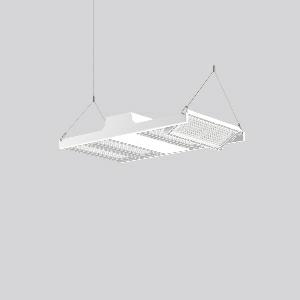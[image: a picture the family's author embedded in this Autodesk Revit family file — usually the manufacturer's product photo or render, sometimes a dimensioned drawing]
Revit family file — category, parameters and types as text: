
# Revit family: light_case_921688_002_76_3383
name_source: partatom
category: Lighting Fixtures
units: mm (PartAtom-declared; Revit-internal decimal feet)

## family parameters
Cut with Voids When Loaded = No
Host = Face
Light Source = No
Part Type = Normal
Room Calculation Point = No
Round Connector Dimension = Use Diameter
Shared = No

## types (1)
- LIGHT CASE (1 x LED Modul 840, 8900 lm, 4000)
    Apparent Load = 225 VA
    CIE Flux Codes = 81 98 100 100 100
    Color Rendering = 80
    Color Temperature = 4000
    Default Elevation = 1800 mm
    Description = Series: LIGHT CASE
Flat highbay luminaire for chain or cable suspension with 4 LED modules that can be swivelled. Housing: die cast aluminium and sheet steel, powder-coated. Optimised thermal management thanks to special luminaire design. Self-cleaning heat sink for constant heat dissipation. Cover: plastic (polycarbonate, shockproof), with integrated four-row lens system. LED modules can be swivelled ± 30° for optimum illumination. Suitable for chain or steel cable suspension (to be provided on site). With 5-pin connection terminal (1.5 m). With integrated movement sensor and light sensor for daylight detection on request. Ball impact proof in accordance with DIN 18032-03 (except steel cable suspension). Luminaire with limited surface temperature in accordance with EN 60598-2-24 for use in environments in which a deposit of conductive dust on the luminaire can be expected. 
Colour: white
Length: 680 mm
Width: 397 mm
Height: 110 mm
Lamp: LED
Socket: without socket
Colour temperature: 4000K
Colour rendering index (CRI): 80
System power: 225 W
Rated luminous flux: 35600 lm
Luminous efficiency: 158 lm/W
Control gear: Converter, dimmable, DALI
Protection class: I
Type of protection: IP 65
    Height = 110 mm
    Lamp = 1 x LED Modul 840
    Lamp Light Flux = 8900 lm
    Lamp count = 1
    Length = 680 mm
    Lifetime = 50000 h
    Luminous efficacy = 158 lm/W
    Manufacturer = RZB
    ModVariant = No
    Model = 921688.002.76
    Mounting Place = Ceiling
    Mounting Type = Pendant
    Number of Poles = 1
    OnlyDefault = Yes
    Power Factor = 1
    Product Name = LIGHT CASE
    Product group = Pendant commercial luminaires
    ProductGroupID = 903
    Protection Class = Protection class I
    Protection Degree = IP 65
    RLX_Detail_Level = 1
    RLX_Emergency_Light_Flux = 0 lm
    RLX_Emergency_Type = 0
    RLX_Emergency_Type_DB = No
    RlxData = <blob elided: 26761 chars, md5=584c3123>
    Socket = socket
    Standby Power = 0 W
    System Light Flux = 35600 lm
    System Power = 225 W
    Type Comments = Product without accessories
    Type Image = 921523.002.76.jpg
    URL = http://relux.com
    VarID = ---
    Voltage = 230 V
    Voltage Range = 220-240 V
    Weight = 0.00 kg
    Width = 397 mm

## geometry (parser evidence)
native form markers: Blend x4, Sweep x21
no freeform markers — native parametric forms only
